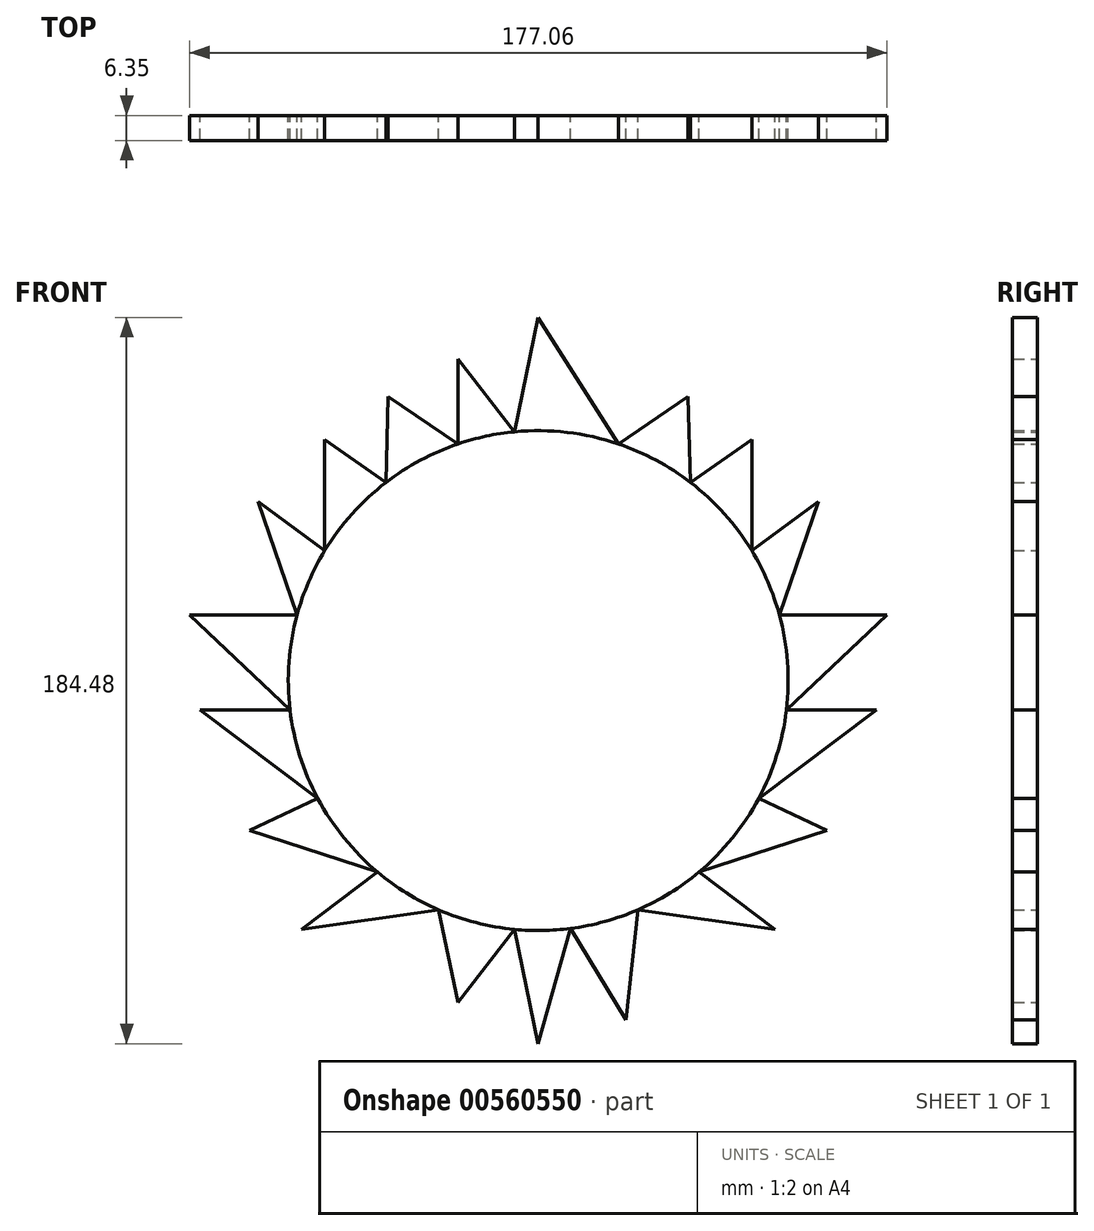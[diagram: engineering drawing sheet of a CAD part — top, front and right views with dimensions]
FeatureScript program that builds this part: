
annotation { "Feature Type Name" : "Feature", "Feature Type Description" : "" }
export const myFeature = defineFeature(function(context is Context, id is Id, definition is map)
    precondition{}
    {
        {
            var Q0;
            Q0=qCreatedBy(makeId("Front.planeOp"),FACE);
            var sketch = newSketch(context, id + "F0", { "sketchPlane" : qUnion([Q0])});
            skCircle(sketch, "E0", {"center": v(0, 0) * mm, "radius": 63.5 * mm});
            skLineSegment(sketch, "E1", {"start": v(-54.25, 33) * mm, "end": v(-54.25, 61.2) * mm});
            skLineSegment(sketch, "E2", {"start": v(-54.25, 61.2) * mm, "end": v(-38.73, 50.32) * mm});
            skLineSegment(sketch, "E3", {"start": v(-38.73, 50.32) * mm, "end": v(-38.73, 50.32) * mm});
            skLineSegment(sketch, "E4", {"start": v(-38.1, 72.23) * mm, "end": v(-38.73, 50.32) * mm});
            skLineSegment(sketch, "E5", {"start": v(-38.1, 72.23) * mm, "end": v(-20.37, 60.14) * mm});
            skLineSegment(sketch, "E6", {"start": v(-20.37, 60.14) * mm, "end": v(-20.37, 81.68) * mm});
            skLineSegment(sketch, "E7", {"start": v(-20.37, 81.68) * mm, "end": v(-20.37, 81.68) * mm});
            skLineSegment(sketch, "E8", {"start": v(-54.25, 33) * mm, "end": v(-71.2, 45.45) * mm});
            skLineSegment(sketch, "E9", {"start": v(-71.2, 45.45) * mm, "end": v(-71.2, 45.45) * mm});
            skLineSegment(sketch, "E10", {"start": v(-71.2, 45.45) * mm, "end": v(-61.27, 16.7) * mm});
            skLineSegment(sketch, "E11", {"start": v(-61.27, 16.7) * mm, "end": v(-88.53, 16.7) * mm});
            skLineSegment(sketch, "E12", {"start": v(-88.53, 16.7) * mm, "end": v(-63.06, -7.5) * mm});
            skLineSegment(sketch, "E13", {"start": v(-63.06, -7.5) * mm, "end": v(-85.9, -7.5) * mm});
            skLineSegment(sketch, "E14", {"start": v(-85.9, -7.5) * mm, "end": v(-56.02, -29.9) * mm});
            skLineSegment(sketch, "E15", {"start": v(-56.02, -29.9) * mm, "end": v(-56.02, -29.9) * mm});
            skLineSegment(sketch, "E16", {"start": v(-73.3, -38.05) * mm, "end": v(-56.02, -29.9) * mm});
            skLineSegment(sketch, "E17", {"start": v(-40.82, -48.64) * mm, "end": v(-60.16, -63.26) * mm});
            skLineSegment(sketch, "E18", {"start": v(-60.16, -63.26) * mm, "end": v(-25.35, -58.22) * mm});
            skLineSegment(sketch, "E19.MirrorCS", {"start": v(38.1, 72.23) * mm, "end": v(20.37, 60.14) * mm});
            skLineSegment(sketch, "E20.MirrorCS", {"start": v(38.1, 72.23) * mm, "end": v(38.73, 50.32) * mm});
            skLineSegment(sketch, "E21.MirrorCS", {"start": v(54.25, 33) * mm, "end": v(54.25, 61.2) * mm});
            skLineSegment(sketch, "E22.MirrorCS", {"start": v(54.25, 61.2) * mm, "end": v(38.73, 50.32) * mm});
            skLineSegment(sketch, "E23.MirrorCS", {"start": v(71.2, 45.45) * mm, "end": v(61.27, 16.7) * mm});
            skLineSegment(sketch, "E24.MirrorCS", {"start": v(40.82, -48.64) * mm, "end": v(60.16, -63.26) * mm});
            skLineSegment(sketch, "E25.MirrorCS", {"start": v(54.25, 33) * mm, "end": v(71.2, 45.45) * mm});
            skLineSegment(sketch, "E26.MirrorCS", {"start": v(61.27, 16.7) * mm, "end": v(88.53, 16.7) * mm});
            skLineSegment(sketch, "E27.MirrorCS", {"start": v(88.53, 16.7) * mm, "end": v(63.06, -7.5) * mm});
            skLineSegment(sketch, "E28.MirrorCS", {"start": v(85.9, -7.5) * mm, "end": v(56.02, -29.9) * mm});
            skLineSegment(sketch, "E29.MirrorCS", {"start": v(63.06, -7.5) * mm, "end": v(85.9, -7.5) * mm});
            skLineSegment(sketch, "E30.MirrorCS", {"start": v(73.3, -38.05) * mm, "end": v(56.02, -29.9) * mm});
            skLineSegment(sketch, "E31.MirrorCS", {"start": v(60.16, -63.26) * mm, "end": v(25.35, -58.22) * mm});
            skPoint(sketch, "E32.start.orphan", {"position": v(0, 80.63) * mm});
            skLineSegment(sketch, "E33", {"start": v(-73.3, -38.05) * mm, "end": v(-40.82, -48.64) * mm});
            skLineSegment(sketch, "E34", {"start": v(73.3, -38.05) * mm, "end": v(40.82, -48.64) * mm});
            skLineSegment(sketch, "E35", {"start": v(-20.37, 81.68) * mm, "end": v(-5.99, 63.22) * mm});
            skLineSegment(sketch, "E36", {"start": v(-5.99, 63.22) * mm, "end": v(0, 92.24) * mm});
            skLineSegment(sketch, "E37", {"start": v(0, 92.24) * mm, "end": v(20.37, 60.14) * mm});
            skPoint(sketch, "E38.MirrorP", {"position": v(0, -80.63) * mm});
            skLineSegment(sketch, "E39.MirrorCS", {"start": v(-5.99, -63.22) * mm, "end": v(0, -92.24) * mm});
            skPoint(sketch, "E40.start.orphan", {"position": v(0, -63.5) * mm});
            skLineSegment(sketch, "E41.MirrorCS", {"start": v(-20.37, -81.68) * mm, "end": v(-5.99, -63.22) * mm});
            skPoint(sketch, "E42.orphan", {"position": v(-166.41, 0) * mm});
            skLineSegment(sketch, "E43", {"start": v(-20.37, -81.68) * mm, "end": v(-25.35, -58.22) * mm});
            skLineSegment(sketch, "E44", {"start": v(0, -92.24) * mm, "end": v(8.2, -62.97) * mm});
            skLineSegment(sketch, "E45", {"start": v(8.2, -62.97) * mm, "end": v(22.26, -86.14) * mm});
            skLineSegment(sketch, "E46", {"start": v(22.26, -86.14) * mm, "end": v(25.35, -58.22) * mm});
            skSolve(sketch);
        }
        {
            var Q0;
            {var subQ0=sQuery(id+"F0.wireOp",EDGE,"E19.MirrorCS");Q0=makeQuery(id+"F0.imprint","IMPRINT",FACE,{"disambiguationData":[TD([[makeQuery(id+"F0.imprint","IMPRINT",EDGE,{"derivedFrom":subQ0}),1.0]])]});}
            var Q1;
            {var subQ0=sQuery(id+"F0.wireOp",EDGE,"E8");Q1=makeQuery(id+"F0.imprint","IMPRINT",FACE,{"disambiguationData":[TD([[makeQuery(id+"F0.imprint","IMPRINT",EDGE,{"derivedFrom":subQ0}),1.0]])]});}
            var Q2;
            {var subQ0=sQuery(id+"F0.wireOp",EDGE,"E21.MirrorCS");Q2=makeQuery(id+"F0.imprint","IMPRINT",FACE,{"disambiguationData":[TD([[makeQuery(id+"F0.imprint","IMPRINT",EDGE,{"derivedFrom":subQ0}),1.0]])]});}
            var Q3;
            {var subQ2=sQuery(id+"F0.wireOp",EDGE,"5864e4f4-c8cc-4152-b7d8-5fe0a2c332290.MirrorCS");Q3=makeQuery(id+"F0.imprint","IMPRINT",FACE,{"disambiguationData":[TD([[makeQuery(id+"F0.imprint","IMPRINT",EDGE,{"derivedFrom":subQ2}),-1.0]])]});}
            var Q4;
            {var subQ0=sQuery(id+"F0.wireOp",EDGE,"E13");Q4=makeQuery(id+"F0.imprint","IMPRINT",FACE,{"disambiguationData":[TD([[makeQuery(id+"F0.imprint","IMPRINT",EDGE,{"derivedFrom":subQ0}),1.0]])]});}
            var Q5;
            {var subQ0=sQuery(id+"F0.wireOp",EDGE,"E0");var subQ7=makeQuery(id+"F0.imprint","INTERSECT",VERTEX,{"derivedFrom":[sQuery(id+"F0.wireOp",EDGE,"ee63edad-4d47-4e86-8511-47d7fe9cd2a1"),subQ0]});Q5=makeQuery(id+"F0.imprint","IMPRINT",FACE,{"disambiguationData":[TD([[makeQuery(id+"F0.imprint","IMPRINT",EDGE,{"disambiguationData":[TD([[subQ7,-1.0]])],"derivedFrom":subQ0}),-1.0]])]});}
            var Q6;
            {var subQ0=sQuery(id+"F0.wireOp",EDGE,"E17");Q6=makeQuery(id+"F0.imprint","IMPRINT",FACE,{"disambiguationData":[TD([[makeQuery(id+"F0.imprint","IMPRINT",EDGE,{"derivedFrom":subQ0}),1.0]])]});}
            var Q7;
            {var subQ0=sQuery(id+"F0.wireOp",EDGE,"E26.MirrorCS");Q7=makeQuery(id+"F0.imprint","IMPRINT",FACE,{"disambiguationData":[TD([[makeQuery(id+"F0.imprint","IMPRINT",EDGE,{"derivedFrom":subQ0}),-1.0]])]});}
            var Q8;
            {var subQ0=sQuery(id+"F0.wireOp",EDGE,"E29.MirrorCS");Q8=makeQuery(id+"F0.imprint","IMPRINT",FACE,{"disambiguationData":[TD([[makeQuery(id+"F0.imprint","IMPRINT",EDGE,{"derivedFrom":subQ0}),-1.0]])]});}
            var Q9;
            {var subQ0=sQuery(id+"F0.wireOp",EDGE,"E11");Q9=makeQuery(id+"F0.imprint","IMPRINT",FACE,{"disambiguationData":[TD([[makeQuery(id+"F0.imprint","IMPRINT",EDGE,{"derivedFrom":subQ0}),1.0]])]});}
            var Q10;
            {var subQ0=sQuery(id+"F0.wireOp",EDGE,"E6");Q10=makeQuery(id+"F0.imprint","IMPRINT",FACE,{"disambiguationData":[TD([[makeQuery(id+"F0.imprint","IMPRINT",EDGE,{"derivedFrom":subQ0}),-1.0]])]});}
            var Q11;
            {var subQ0=sQuery(id+"F0.wireOp",EDGE,"E1");Q11=makeQuery(id+"F0.imprint","IMPRINT",FACE,{"disambiguationData":[TD([[makeQuery(id+"F0.imprint","IMPRINT",EDGE,{"derivedFrom":subQ0}),-1.0]])]});}
            var Q12;
            {var subQ0=sQuery(id+"F0.wireOp",EDGE,"E23.MirrorCS");Q12=makeQuery(id+"F0.imprint","IMPRINT",FACE,{"disambiguationData":[TD([[makeQuery(id+"F0.imprint","IMPRINT",EDGE,{"derivedFrom":subQ0}),-1.0]])]});}
            var Q13;
            {var subQ0=sQuery(id+"F0.wireOp",EDGE,"58a78bd1-18de-422e-9189-13f51e26cda7");Q13=makeQuery(id+"F0.imprint","IMPRINT",FACE,{"disambiguationData":[TD([[makeQuery(id+"F0.imprint","IMPRINT",EDGE,{"derivedFrom":subQ0}),-1.0]])]});}
            var Q14;
            {var subQ0=sQuery(id+"F0.wireOp",EDGE,"E24.MirrorCS");Q14=makeQuery(id+"F0.imprint","IMPRINT",FACE,{"disambiguationData":[TD([[makeQuery(id+"F0.imprint","IMPRINT",EDGE,{"derivedFrom":subQ0}),-1.0]])]});}
            var Q15;
            {var subQ0=sQuery(id+"F0.wireOp",EDGE,"2d02d5e7-dd58-4d07-8821-be89939fdbc80.MirrorCS");Q15=makeQuery(id+"F0.imprint","IMPRINT",FACE,{"disambiguationData":[TD([[makeQuery(id+"F0.imprint","IMPRINT",EDGE,{"derivedFrom":subQ0}),1.0]])]});}
            var Q16;
            {var subQ0=sQuery(id+"F0.wireOp",EDGE,"E4");Q16=makeQuery(id+"F0.imprint","IMPRINT",FACE,{"disambiguationData":[TD([[makeQuery(id+"F0.imprint","IMPRINT",EDGE,{"derivedFrom":subQ0}),1.0]])]});}
            extrude(context, id + "F1", {"entities" : qUnion([Q0, Q1, Q2, Q3, Q4, Q5, Q6, Q7, Q8, Q9, Q10, Q11, Q12, Q13, Q14, Q15, Q16]), "depth" : 6.35 * mm, "offsetDistance" : 25.4 * mm});
        }
        {
            var Q0;
            {var subQ0=sQuery(id+"F0.wireOp",EDGE,"E16");Q0=makeQuery(id+"F0.imprint","IMPRINT",FACE,{"disambiguationData":[TD([[makeQuery(id+"F0.imprint","IMPRINT",EDGE,{"derivedFrom":subQ0}),-1.0]])]});}
            var Q1;
            {var subQ0=sQuery(id+"F0.wireOp",EDGE,"E30.MirrorCS");Q1=makeQuery(id+"F0.imprint","IMPRINT",FACE,{"disambiguationData":[TD([[makeQuery(id+"F0.imprint","IMPRINT",EDGE,{"derivedFrom":subQ0}),1.0]])]});}
            extrude(context, id + "F2", {"entities" : qUnion([Q0, Q1]), "operationType" : NewBodyOperationType.ADD, "depth" : 6.35 * mm, "offsetDistance" : 25.4 * mm});
        }
        {
            var Q0;
            {var subQ2=sQuery(id+"F0.wireOp",EDGE,"E39.MirrorCS");Q0=makeQuery(id+"F0.imprint","IMPRINT",FACE,{"disambiguationData":[TD([[makeQuery(id+"F0.imprint","IMPRINT",EDGE,{"derivedFrom":subQ2}),1.0]])]});}
            var Q1;
            {var subQ2=sQuery(id+"F0.wireOp",EDGE,"E36");Q1=makeQuery(id+"F0.imprint","IMPRINT",FACE,{"disambiguationData":[TD([[makeQuery(id+"F0.imprint","IMPRINT",EDGE,{"derivedFrom":subQ2}),-1.0]])]});}
            extrude(context, id + "F3", {"entities" : qUnion([Q0, Q1]), "operationType" : NewBodyOperationType.ADD, "depth" : 6.35 * mm, "offsetDistance" : 25.4 * mm});
        }
        {
            var Q0;
            {var subQ2=sQuery(id+"F0.wireOp",EDGE,"E41.MirrorCS");Q0=makeQuery(id+"F0.imprint","IMPRINT",FACE,{"disambiguationData":[TD([[makeQuery(id+"F0.imprint","IMPRINT",EDGE,{"derivedFrom":subQ2}),1.0]])]});}
            var Q1;
            {var subQ0=sQuery(id+"F0.wireOp",EDGE,"E24.MirrorCS");Q1=makeQuery(id+"F0.imprint","IMPRINT",FACE,{"disambiguationData":[TD([[makeQuery(id+"F0.imprint","IMPRINT",EDGE,{"derivedFrom":subQ0}),-1.0]])]});}
            extrude(context, id + "F4", {"entities" : qUnion([Q0, Q1]), "operationType" : NewBodyOperationType.ADD, "depth" : 6.35 * mm, "offsetDistance" : 25.4 * mm});
        }
        {
            var Q0;
            {var subQ2=sQuery(id+"F0.wireOp",EDGE,"E45");Q0=makeQuery(id+"F0.imprint","IMPRINT",FACE,{"disambiguationData":[TD([[makeQuery(id+"F0.imprint","IMPRINT",EDGE,{"derivedFrom":subQ2}),1.0]])]});}
            extrude(context, id + "F5", {"entities" : qUnion([Q0]), "operationType" : NewBodyOperationType.ADD, "depth" : 6.35 * mm, "offsetDistance" : 25.4 * mm});
        }
    });
